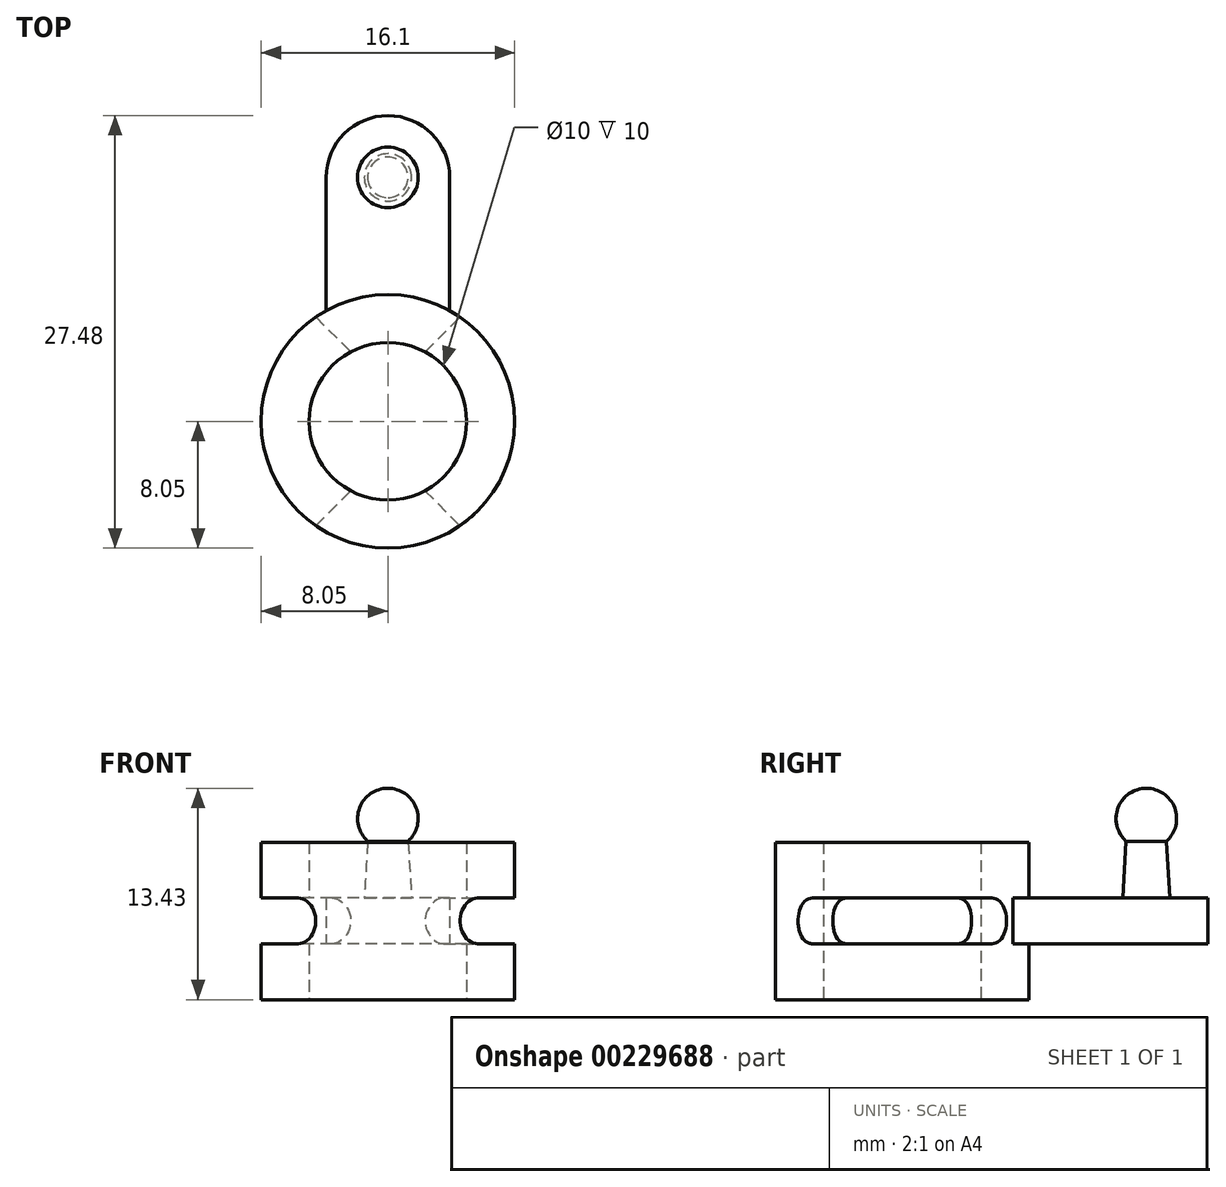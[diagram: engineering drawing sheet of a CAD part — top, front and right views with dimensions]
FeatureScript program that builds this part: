
annotation { "Feature Type Name" : "Feature", "Feature Type Description" : "" }
export const myFeature = defineFeature(function(context is Context, id is Id, definition is map)
    precondition{}
    {
        {
            var Q0;
            Q0=qCreatedBy(makeId("Top.planeOp"),FACE);
            var sketch = newSketch(context, id + "F0", { "sketchPlane" : qUnion([Q0])});
            skCircle(sketch, "E0", {"center": v(0, 0) * mm, "radius": 4.95 * mm});
            skCircle(sketch, "E1", {"center": v(0, 0) * mm, "radius": 8.05 * mm});
            skArc(sketch, "E2", {"start": v(3.92, 15.5) * mm, "mid": v(0, 19.42) * mm, "end": v(-3.92, 15.5) * mm});
            skLineSegment(sketch, "E3", {"start": v(-3.92, 15.5) * mm, "end": v(-3.92, 7.03) * mm});
            skLineSegment(sketch, "E4", {"start": v(0, 0) * mm, "end": v(0, 15.5) * mm, "construction": true});
            skLineSegment(sketch, "E5.MirrorCS", {"start": v(3.93, 15.5) * mm, "end": v(3.92, 7.03) * mm});
            skSolve(sketch);
        }
        {
            var Q0;
            Q0=makeQuery(id+"F0.imprint","IMPRINT",FACE,{"disambiguationData":[TD([[makeQuery(id+"F0.imprint","IMPRINT",EDGE,{"derivedFrom":sQuery(id+"F0.wireOp",EDGE,"E2")}),1.0]])]});
            extrude(context, id + "F1", {"entities" : qUnion([Q0]), "endBound" : BoundingType.SYMMETRIC, "depth" : 2.9 * mm});
        }
        {
            var Q0;
            Q0=qCreatedBy(makeId("Top.planeOp"),FACE);
            var sketch = newSketch(context, id + "F2", { "sketchPlane" : qUnion([Q0])});
            skCircle(sketch, "E6", {"center": v(0, 0) * mm, "radius": 8.05 * mm});
            skCircle(sketch, "E7", {"center": v(0, 0) * mm, "radius": 5 * mm});
            skSolve(sketch);
        }
        {
            var Q0;
            Q0=makeQuery(id+"F2.imprint","IMPRINT",FACE,{"disambiguationData":[TD([[makeQuery(id+"F2.imprint","IMPRINT",EDGE,{"derivedFrom":sQuery(id+"F2.wireOp",EDGE,"E6")}),1.0]])]});
            extrude(context, id + "F3", {"entities" : qUnion([Q0]), "operationType" : NewBodyOperationType.ADD, "endBound" : BoundingType.SYMMETRIC, "depth" : 10 * mm});
        }
        {
            var Q0;
            Q0=qCreatedBy(makeId("Front.planeOp"),FACE);
            var sketch = newSketch(context, id + "F4", { "sketchPlane" : qUnion([Q0])});
            skLineSegment(sketch, "E8.right", {"start": v(-8.05, -1.45) * mm, "end": v(-8.05, 1.45) * mm});
            skLineSegment(sketch, "E9", {"start": v(-4.95, 1.45) * mm, "end": v(-4.95, -1.45) * mm});
            skLineSegment(sketch, "E10.trimOffspring", {"start": v(-4.95, 1.45) * mm, "end": v(-8.05, 1.45) * mm});
            skLineSegment(sketch, "E11.trimOffspring", {"start": v(-4.95, -1.45) * mm, "end": v(-8.05, -1.45) * mm});
            skLineSegment(sketch, "E12", {"start": v(0, 2.4) * mm, "end": v(0, -2.96) * mm, "construction": true});
            skLineSegment(sketch, "E13.MirrorCS", {"start": v(8.05, -1.45) * mm, "end": v(8.05, 1.45) * mm});
            skLineSegment(sketch, "E14.MirrorCS", {"start": v(4.95, 1.45) * mm, "end": v(8.05, 1.45) * mm});
            skLineSegment(sketch, "E15.MirrorCS", {"start": v(4.95, 1.45) * mm, "end": v(4.95, -1.45) * mm});
            skLineSegment(sketch, "E16.MirrorCS", {"start": v(4.95, -1.45) * mm, "end": v(8.05, -1.45) * mm});
            skSolve(sketch);
        }
        {
            var Q0;
            Q0=qCreatedBy(makeId("Front.planeOp"),FACE);
            var sketch = newSketch(context, id + "F5", { "sketchPlane" : qUnion([Q0])});
            skLineSegment(sketch, "E17", {"start": v(0, -15.74) * mm, "end": v(0, 16.07) * mm, "construction": true});
            skSolve(sketch);
        }
        {
            var Q0;
            Q0 = qSketchRegion(id + "F4", true);
            var Q1;
            Q1=sQuery(id+"F5.wireOp",EDGE,"E17");
            revolve(context, id + "F6", {"operationType" : NewBodyOperationType.REMOVE, "entities" : qUnion([Q0]), "axis" : qUnion([Q1]), "revolveType" : RevolveType.SYMMETRIC, "oppositeDirection" : true, "angle" : 90 * degree});
        }
        {
            var Q0;
            Q0=qCreatedBy(makeId("Right.planeOp"),FACE);
            var sketch = newSketch(context, id + "F7", { "sketchPlane" : qUnion([Q0])});
            skLineSegment(sketch, "E18", {"start": v(15.5, 0) * mm, "end": v(15.5, 6.5) * mm});
            skArc(sketch, "E19", {"start": v(15.5, 8.43) * mm, "mid": v(13.7, 7.19) * mm, "end": v(14.22, 5.07) * mm});
            skLineSegment(sketch, "E20", {"start": v(14.22, 5.07) * mm, "end": v(14, 1.45) * mm});
            skLineSegment(sketch, "E21", {"start": v(14, 1.45) * mm, "end": v(15.5, 1.45) * mm});
            skLineSegment(sketch, "E22", {"start": v(15.5, 6.5) * mm, "end": v(15.5, 8.43) * mm});
            skSolve(sketch);
        }
        {
            var Q0;
            Q0=makeQuery(id+"F7.imprint","IMPRINT",FACE,{"disambiguationData":[TD([[makeQuery(id+"F7.imprint","IMPRINT",EDGE,{"derivedFrom":sQuery(id+"F7.wireOp",EDGE,"E19")}),1.0]])]});
            var Q1;
            Q1=sQuery(id+"F7.wireOp",EDGE,"E18");
            revolve(context, id + "F8", {"operationType" : NewBodyOperationType.ADD, "entities" : qUnion([Q0]), "axis" : qUnion([Q1]), "revolveType" : RevolveType.FULL});
        }
        {
            var Q0;
            Q0=qCreatedBy(makeId("Top.planeOp"),FACE);
            var sketch = newSketch(context, id + "F9", { "sketchPlane" : qUnion([Q0])});
            skLineSegment(sketch, "E23", {"start": v(0, 0) * mm, "end": v(7.95, 7.95) * mm, "construction": true});
            skSolve(sketch);
        }
        {
            var Q0;
            Q0=sQuery(id+"F9.wireOp",VERTEX,"E23.end");
            var Q1;
            Q1=sQuery(id+"F9.wireOp",EDGE,"E23");
            cPlane(context, id + "F10", {"entities" : qUnion([Q0, Q1]), "cplaneType" : CPlaneType.LINE_POINT, "offset" : 25 * mm, "width" : 150 * mm, "height" : 150 * mm});
        }
        {
            var Q0;
            Q0=qCreatedBy(id+"F10.planeOp",FACE);
            var sketch = newSketch(context, id + "F11", { "sketchPlane" : qUnion([Q0])});
            skCircle(sketch, "E24", {"center": v(0, 0) * mm, "radius": 1.45 * mm});
            skSolve(sketch);
        }
        {
            var Q0;
            Q0=makeQuery(id+"F11.imprint","IMPRINT",FACE,{"disambiguationData":[TD([[makeQuery(id+"F11.imprint","IMPRINT",EDGE,{"derivedFrom":sQuery(id+"F11.wireOp",EDGE,"E24")}),1.0]])]});
            extrude(context, id + "F12", {"entities" : qUnion([Q0]), "operationType" : NewBodyOperationType.REMOVE, "oppositeDirection" : true, "depth" : 25 * mm});
        }
        {
            var Q0;
            Q0=sQuery(id+"F9.wireOp",EDGE,"E23");
            cPlane(context, id + "F13", {"entities" : qUnion([Q0]), "cplaneType" : CPlaneType.LINE_ANGLE, "offset" : 25 * mm, "angle" : 90 * degree, "width" : 150 * mm, "height" : 150 * mm});
        }
        {
            var Q0;
            Q0=qCreatedBy(id+"F13.planeOp",FACE);
            var sketch = newSketch(context, id + "F14", { "sketchPlane" : qUnion([Q0])});
            skCircle(sketch, "E25", {"center": v(0, 0) * mm, "radius": 1.45 * mm});
            skSolve(sketch);
        }
        {
            var Q0;
            Q0=makeQuery(id+"F14.imprint","IMPRINT",FACE,{"disambiguationData":[TD([[makeQuery(id+"F14.imprint","IMPRINT",EDGE,{"derivedFrom":sQuery(id+"F14.wireOp",EDGE,"E25")}),1.0]])]});
            extrude(context, id + "F15", {"entities" : qUnion([Q0]), "operationType" : NewBodyOperationType.REMOVE, "endBound" : BoundingType.SYMMETRIC, "oppositeDirection" : true, "depth" : 25 * mm});
        }
    });
